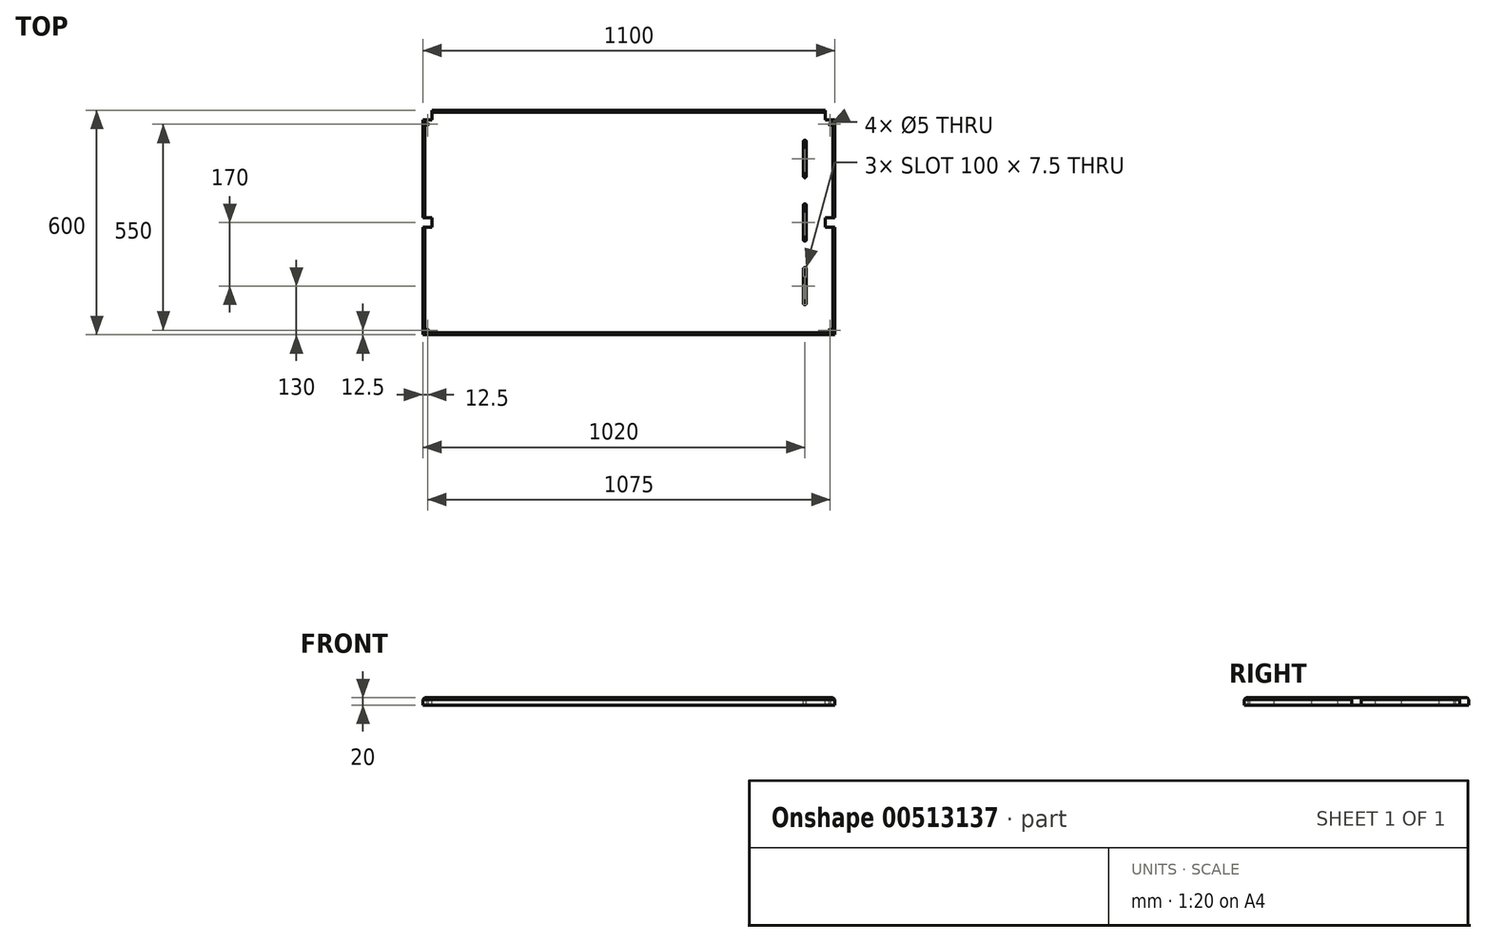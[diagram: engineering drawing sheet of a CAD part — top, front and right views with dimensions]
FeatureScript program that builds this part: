
annotation { "Feature Type Name" : "Feature", "Feature Type Description" : "" }
export const myFeature = defineFeature(function(context is Context, id is Id, definition is map)
    precondition{}
    {
        {
            var Q0;
            Q0=qCreatedBy(makeId("Top.planeOp"),FACE);
            var sketch = newSketch(context, id + "F0", { "sketchPlane" : qUnion([Q0])});
            skLineSegment(sketch, "E0.bottom", {"start": v(550, 300) * mm, "end": v(-550, 300) * mm});
            skLineSegment(sketch, "E0.top", {"start": v(550, -300) * mm, "end": v(-550, -300) * mm});
            skLineSegment(sketch, "E0.left", {"start": v(550, 300) * mm, "end": v(550, -300) * mm});
            skLineSegment(sketch, "E0.right", {"start": v(-550, 300) * mm, "end": v(-550, -300) * mm});
            skPoint(sketch, "E0.middle", {"position": v(0, 0) * mm});
            skSolve(sketch);
        }
        {
            var Q0;
            Q0=makeQuery(id+"F0.imprint","IMPRINT",FACE,{"disambiguationData":[TD([[makeQuery(id+"F0.imprint","IMPRINT",EDGE,{"derivedFrom":sQuery(id+"F0.wireOp",EDGE,"E0.bottom")}),1.0]])]});
            extrude(context, id + "F1", {"entities" : qUnion([Q0]), "depth" : 20 * mm, "offsetDistance" : 25 * mm});
        }
        {
            var Q0;
            Q0=makeQuery(id+"F1.opExtrude","CAP_FACE",FACE,{"disambiguationData":[OSD([sQuery(id+"F0.wireOp",EDGE,"E0.bottom"),sQuery(id+"F0.wireOp",EDGE,"E0.top"),sQuery(id+"F0.wireOp",EDGE,"E0.left"),sQuery(id+"F0.wireOp",EDGE,"E0.right")])],"isStart":false});
            var sketch = newSketch(context, id + "F2", { "sketchPlane" : qUnion([Q0])});
            skLineSegment(sketch, "E1", {"start": v(550, 0) * mm, "end": v(390, 0) * mm, "construction": true});
            skPoint(sketch, "E1.endSnap0", {"position": v(550, 0) * mm});
            skLineSegment(sketch, "E2", {"start": v(470, 300) * mm, "end": v(470, -300) * mm, "construction": true});
            skPoint(sketch, "E2.startSnap0", {"position": v(470, 0) * mm});
            skLineSegment(sketch, "E3.bottom", {"start": v(470, -120) * mm, "end": v(470, -120) * mm});
            skLineSegment(sketch, "E3.top", {"start": v(470, -220) * mm, "end": v(470, -220) * mm});
            skLineSegment(sketch, "E3.left", {"start": v(473.75, -123.75) * mm, "end": v(473.75, -216.25) * mm});
            skLineSegment(sketch, "E3.right", {"start": v(466.25, -123.75) * mm, "end": v(466.25, -216.25) * mm});
            skPoint(sketch, "E3.middle", {"position": v(470, -170) * mm});
            skLineSegment(sketch, "E4.bottom", {"start": v(470, 50) * mm, "end": v(470, 50) * mm});
            skLineSegment(sketch, "E4.top", {"start": v(470, -50) * mm, "end": v(470, -50) * mm});
            skLineSegment(sketch, "E4.left", {"start": v(473.75, 46.25) * mm, "end": v(473.75, -46.25) * mm});
            skLineSegment(sketch, "E4.right", {"start": v(466.25, 46.25) * mm, "end": v(466.25, -46.25) * mm});
            skPoint(sketch, "E5.MirrorP", {"position": v(470, 170) * mm});
            skLineSegment(sketch, "E6.MirrorCS", {"start": v(466.25, 123.75) * mm, "end": v(466.25, 216.25) * mm});
            skLineSegment(sketch, "E7.MirrorCS", {"start": v(473.75, 123.75) * mm, "end": v(473.75, 216.25) * mm});
            skLineSegment(sketch, "E8.MirrorCS", {"start": v(470, 220) * mm, "end": v(470, 220) * mm});
            skLineSegment(sketch, "E9.MirrorCS", {"start": v(470, 120) * mm, "end": v(470, 120) * mm});
            skPoint(sketch, "E10.visualSharp", {"position": v(466.25, -120) * mm});
            skArc(sketch, "E10.filletArc", {"start": v(470, -120) * mm, "mid": v(467.35, -121.1) * mm, "end": v(466.25, -123.75) * mm});
            skPoint(sketch, "E11.visualSharp", {"position": v(473.75, -120) * mm});
            skArc(sketch, "E11.filletArc", {"start": v(473.75, -123.75) * mm, "mid": v(472.65, -121.1) * mm, "end": v(470, -120) * mm});
            skPoint(sketch, "E12.visualSharp", {"position": v(466.25, -220) * mm});
            skArc(sketch, "E12.filletArc", {"start": v(466.25, -216.25) * mm, "mid": v(467.35, -218.9) * mm, "end": v(470, -220) * mm});
            skPoint(sketch, "E13.visualSharp", {"position": v(473.75, -220) * mm});
            skArc(sketch, "E13.filletArc", {"start": v(470, -220) * mm, "mid": v(472.65, -218.9) * mm, "end": v(473.75, -216.25) * mm});
            skPoint(sketch, "E14.visualSharp", {"position": v(466.25, 50) * mm});
            skArc(sketch, "E14.filletArc", {"start": v(470, 50) * mm, "mid": v(467.35, 48.9) * mm, "end": v(466.25, 46.25) * mm});
            skPoint(sketch, "E15.visualSharp", {"position": v(473.75, 50) * mm});
            skArc(sketch, "E15.filletArc", {"start": v(473.75, 46.25) * mm, "mid": v(472.65, 48.9) * mm, "end": v(470, 50) * mm});
            skPoint(sketch, "E16.visualSharp", {"position": v(466.25, -50) * mm});
            skArc(sketch, "E16.filletArc", {"start": v(466.25, -46.25) * mm, "mid": v(467.35, -48.9) * mm, "end": v(470, -50) * mm});
            skPoint(sketch, "E17.visualSharp", {"position": v(473.75, -50) * mm});
            skArc(sketch, "E17.filletArc", {"start": v(470, -50) * mm, "mid": v(472.65, -48.9) * mm, "end": v(473.75, -46.25) * mm});
            skPoint(sketch, "E18.visualSharp", {"position": v(473.75, 120) * mm});
            skArc(sketch, "E18.filletArc", {"start": v(470, 120) * mm, "mid": v(472.65, 121.1) * mm, "end": v(473.75, 123.75) * mm});
            skPoint(sketch, "E19.visualSharp", {"position": v(466.25, 120) * mm});
            skArc(sketch, "E19.filletArc", {"start": v(466.25, 123.75) * mm, "mid": v(467.35, 121.1) * mm, "end": v(470, 120) * mm});
            skPoint(sketch, "E20.visualSharp", {"position": v(466.25, 220) * mm});
            skArc(sketch, "E20.filletArc", {"start": v(470, 220) * mm, "mid": v(467.35, 218.9) * mm, "end": v(466.25, 216.25) * mm});
            skPoint(sketch, "E21.visualSharp", {"position": v(473.75, 220) * mm});
            skArc(sketch, "E21.filletArc", {"start": v(473.75, 216.25) * mm, "mid": v(472.65, 218.9) * mm, "end": v(470, 220) * mm});
            skLineSegment(sketch, "E22", {"start": v(390, 0) * mm, "end": v(-550, 0) * mm, "construction": true});
            skLineSegment(sketch, "E23.bottom", {"start": v(-525, 12.5) * mm, "end": v(-575, 12.5) * mm});
            skLineSegment(sketch, "E23.top", {"start": v(-525, -12.5) * mm, "end": v(-575, -12.5) * mm});
            skLineSegment(sketch, "E23.left", {"start": v(-525, 12.5) * mm, "end": v(-525, -12.5) * mm});
            skLineSegment(sketch, "E23.right", {"start": v(-575, 12.5) * mm, "end": v(-575, -12.5) * mm});
            skPoint(sketch, "E23.middle", {"position": v(-550, 0) * mm});
            skLineSegment(sketch, "E24.MirrorCS", {"start": v(525, 12.5) * mm, "end": v(525, -12.5) * mm});
            skLineSegment(sketch, "E25.MirrorCS", {"start": v(525, 12.5) * mm, "end": v(575, 12.5) * mm});
            skLineSegment(sketch, "E26.MirrorCS", {"start": v(575, 12.5) * mm, "end": v(575, -12.5) * mm});
            skLineSegment(sketch, "E27.MirrorCS", {"start": v(525, -12.5) * mm, "end": v(575, -12.5) * mm});
            skLineSegment(sketch, "E28.bottom", {"start": v(-550, 300) * mm, "end": v(-525, 300) * mm});
            skLineSegment(sketch, "E28.top", {"start": v(-550, 275) * mm, "end": v(-525, 275) * mm});
            skLineSegment(sketch, "E28.left", {"start": v(-550, 300) * mm, "end": v(-550, 275) * mm});
            skLineSegment(sketch, "E28.right", {"start": v(-525, 300) * mm, "end": v(-525, 275) * mm});
            skLineSegment(sketch, "E29.bottom", {"start": v(550, 300) * mm, "end": v(525, 300) * mm});
            skLineSegment(sketch, "E29.top", {"start": v(550, 275) * mm, "end": v(525, 275) * mm});
            skLineSegment(sketch, "E29.left", {"start": v(550, 300) * mm, "end": v(550, 275) * mm});
            skLineSegment(sketch, "E29.right", {"start": v(525, 300) * mm, "end": v(525, 275) * mm});
            skSolve(sketch);
        }
        {
            var Q0;
            Q0 = qSketchRegion(id + "F2", true);
            extrude(context, id + "F3", {"entities" : qUnion([Q0]), "operationType" : NewBodyOperationType.REMOVE, "endBound" : BoundingType.THROUGH_ALL, "oppositeDirection" : true, "depth" : 25 * mm, "offsetDistance" : 25 * mm});
        }
        {
            var Q0;
            Q0=makeQuery(id+"F1.opExtrude","CAP_FACE",FACE,{"disambiguationData":[OSD([sQuery(id+"F0.wireOp",EDGE,"E0.bottom"),sQuery(id+"F0.wireOp",EDGE,"E0.top"),sQuery(id+"F0.wireOp",EDGE,"E0.left"),sQuery(id+"F0.wireOp",EDGE,"E0.right")])],"isStart":false});
            var sketch = newSketch(context, id + "F4", { "sketchPlane" : qUnion([Q0])});
            skPoint(sketch, "E30", {"position": v(-537.5, -287.5) * mm});
            skPoint(sketch, "E31.MirrorP", {"position": v(537.5, -287.5) * mm});
            skPoint(sketch, "E32", {"position": v(-537.5, 262.5) * mm});
            skPoint(sketch, "E33.MirrorP", {"position": v(537.5, 262.5) * mm});
            skSolve(sketch);
        }
        {
            var Q0;
            Q0=sQuery(id+"F4.wireOp",VERTEX,"E31.MirrorP");
            var Q1;
            Q1=sQuery(id+"F4.wireOp",VERTEX,"E30");
            var Q2;
            Q2=sQuery(id+"F4.wireOp",VERTEX,"E33.MirrorP");
            var Q3;
            Q3=sQuery(id+"F4.wireOp",VERTEX,"E32");
            var Q4;
            Q4=makeQuery(id+"F1.opExtrude","SWEPT_BODY",BODY,{"disambiguationData":[OSD([sQuery(id+"F0.wireOp",EDGE,"E0.bottom"),sQuery(id+"F0.wireOp",EDGE,"E0.top"),sQuery(id+"F0.wireOp",EDGE,"E0.left"),sQuery(id+"F0.wireOp",EDGE,"E0.right")])]});
            hole(context, id + "F5", {"style" : HoleStyle.SIMPLE, "endStyle" : HoleEndStyle.THROUGH, "holeDiameter" : 5 * mm, "isTappedThrough" : true, "tappedDepth" : 12 * mm, "tapClearance" : 3, "startFromSketch" : true, "locations" : qUnion([Q0, Q1, Q2, Q3]), "scope" : qUnion([Q4])});
        }
        {
            var Q0;
            Q0=makeQuery(id+"F1.opExtrude","CAP_EDGE",EDGE,{"disambiguationData":[OSD([sQuery(id+"F0.wireOp",EDGE,"E0.top")])],"isStart":false});
            var Q1;
            Q1=makeQuery(id+"F1.opExtrude","CAP_EDGE",EDGE,{"disambiguationData":[OSD([sQuery(id+"F0.wireOp",EDGE,"E0.right")])],"isStart":false});
            var Q2;
            Q2=makeQuery(id+"F1.opExtrude","CAP_EDGE",EDGE,{"disambiguationData":[OSD([sQuery(id+"F0.wireOp",EDGE,"E0.bottom")])],"isStart":false});
            var Q3;
            Q3=makeQuery(id+"F1.opExtrude","CAP_EDGE",EDGE,{"disambiguationData":[OSD([sQuery(id+"F0.wireOp",EDGE,"E0.left")])],"isStart":false});
            chamfer(context, id + "F6", {"entities" : qUnion([Q0, Q1, Q2, Q3]), "width" : 5 * mm, "tangentPropagation" : true});
        }
    });
